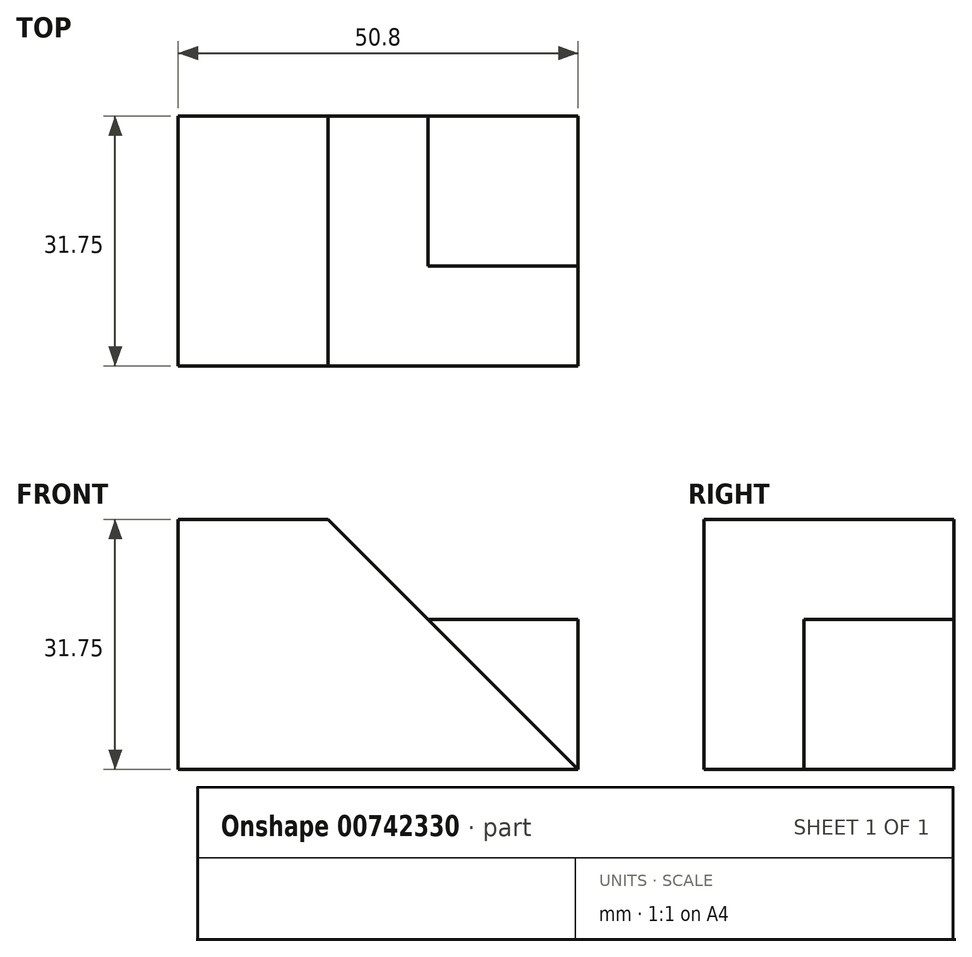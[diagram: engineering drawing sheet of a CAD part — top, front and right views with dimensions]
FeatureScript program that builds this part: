
annotation { "Feature Type Name" : "Feature", "Feature Type Description" : "" }
export const myFeature = defineFeature(function(context is Context, id is Id, definition is map)
    precondition{}
    {
        {
            var Q0;
            Q0=qCreatedBy(makeId("Front.planeOp"),FACE);
            var sketch = newSketch(context, id + "F0", { "sketchPlane" : qUnion([Q0])});
            skLineSegment(sketch, "E0", {"start": v(0, 0) * mm, "end": v(-50.8, 0) * mm});
            skLineSegment(sketch, "E1", {"start": v(-50.8, 0) * mm, "end": v(-50.8, 31.75) * mm});
            skLineSegment(sketch, "E2", {"start": v(-50.8, 31.75) * mm, "end": v(0, 31.75) * mm});
            skLineSegment(sketch, "E3", {"start": v(0, 31.75) * mm, "end": v(0, 0) * mm});
            skSolve(sketch);
        }
        {
            var Q0;
            Q0 = qSketchRegion(id + "F0", true);
            extrude(context, id + "F1", {"entities" : qUnion([Q0]), "depth" : 31.75 * mm, "offsetDistance" : 25.4 * mm});
        }
        {
            var Q0;
            Q0=makeQuery(id+"F1.opExtrude","CAP_FACE",FACE,{"disambiguationData":[OSD([sQuery(id+"F0.wireOp",EDGE,"E0"),sQuery(id+"F0.wireOp",EDGE,"E1"),sQuery(id+"F0.wireOp",EDGE,"E2"),sQuery(id+"F0.wireOp",EDGE,"E3")])],"isStart":false});
            var sketch = newSketch(context, id + "F2", { "sketchPlane" : qUnion([Q0])});
            skLineSegment(sketch, "E4", {"start": v(-31.75, 31.75) * mm, "end": v(0, 0) * mm});
            skSolve(sketch);
        }
        {
            var Q0;
            Q0 = qSketchRegion(id + "F2", true);
            var Q1;
            {var subQ0=sQuery(id+"F2.wireOp",EDGE,"E4");Q1=makeQuery(id+"F2.imprint","IMPRINT",FACE,{"disambiguationData":[TD([[makeQuery(id+"F2.imprint","IMPRINT",EDGE,{"derivedFrom":subQ0}),1.0]])]});}
            extrude(context, id + "F3", {"entities" : qUnion([Q0, Q1]), "operationType" : NewBodyOperationType.REMOVE, "oppositeDirection" : true, "depth" : 12.7 * mm, "offsetDistance" : 25.4 * mm});
        }
        {
            var Q0;
            Q0=makeQuery(id+"F3.boolean.opBoolean","COPY",FACE,{"derivedFrom":makeQuery(id+"F3.opExtrude","CAP_FACE",FACE,{"disambiguationData":[OSD([sQuery(id+"F0.wireOp",EDGE,"E2"),sQuery(id+"F0.wireOp",EDGE,"E3"),sQuery(id+"F2.wireOp",EDGE,"E4")])],"isStart":false})});
            var sketch = newSketch(context, id + "F4", { "sketchPlane" : qUnion([Q0])});
            skLineSegment(sketch, "E5", {"start": v(-19.05, 19.05) * mm, "end": v(0, 19.05) * mm});
            skSolve(sketch);
        }
        {
            var Q0;
            Q0 = qSketchRegion(id + "F4", true);
            var Q1;
            {var subQ0=sQuery(id+"F4.wireOp",EDGE,"E5");Q1=makeQuery(id+"F4.imprint","IMPRINT",FACE,{"disambiguationData":[TD([[makeQuery(id+"F4.imprint","IMPRINT",EDGE,{"derivedFrom":subQ0}),1.0]])]});}
            extrude(context, id + "F5", {"entities" : qUnion([Q0, Q1]), "operationType" : NewBodyOperationType.REMOVE, "endBound" : BoundingType.THROUGH_ALL, "oppositeDirection" : true, "depth" : 25.4 * mm, "offsetDistance" : 25.4 * mm});
        }
    });
